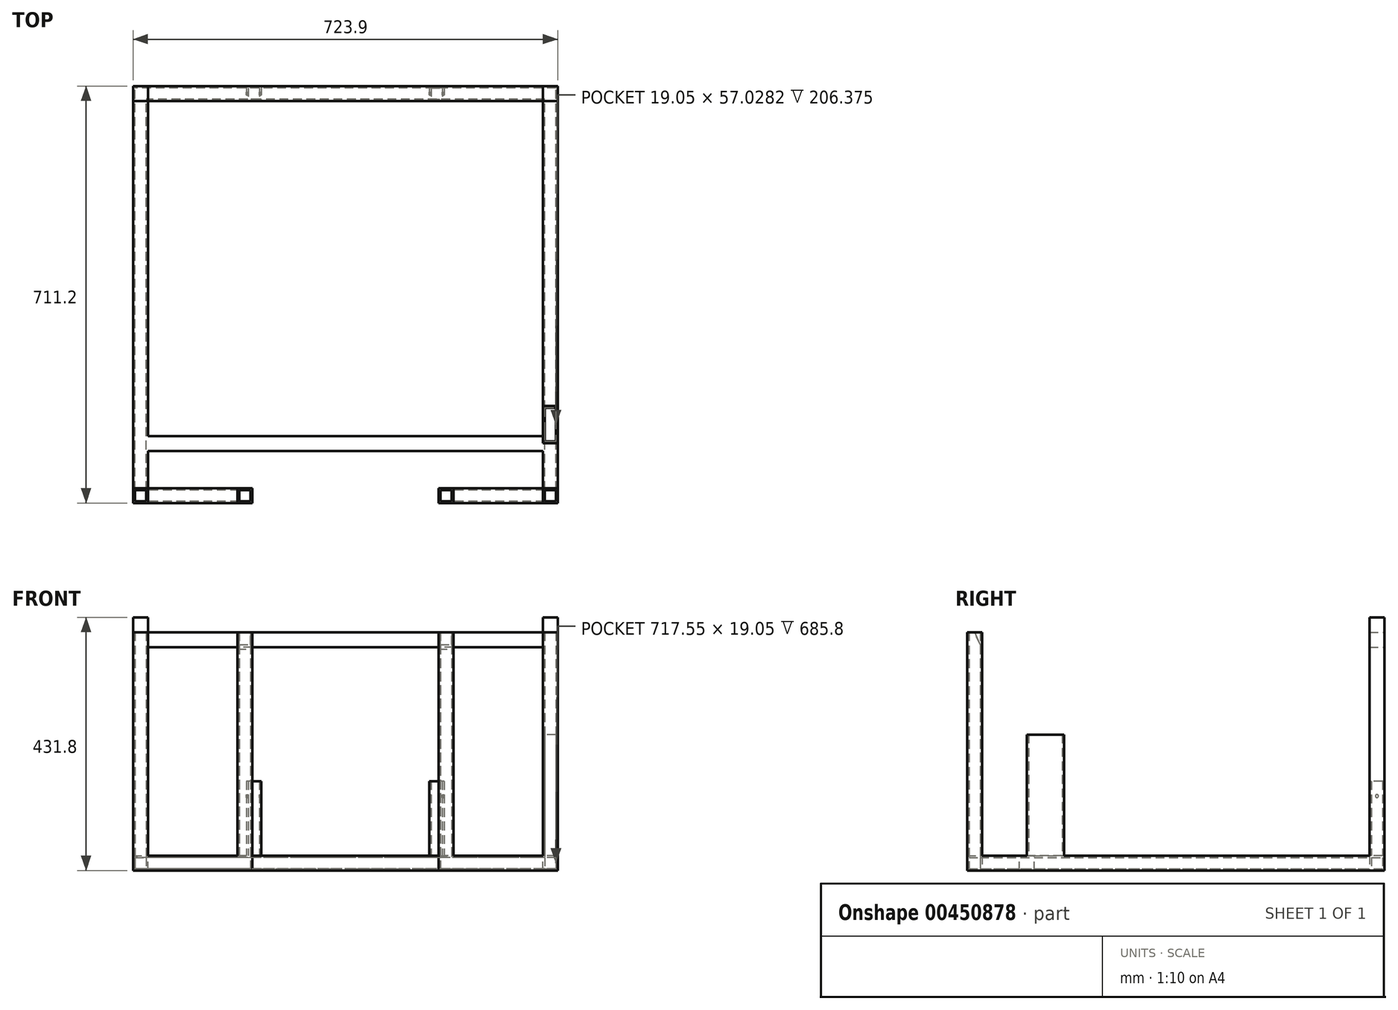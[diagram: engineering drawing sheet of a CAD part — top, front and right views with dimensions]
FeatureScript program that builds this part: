
annotation { "Feature Type Name" : "Feature", "Feature Type Description" : "" }
export const myFeature = defineFeature(function(context is Context, id is Id, definition is map)
    precondition{}
    {
        {
            var Q0;
            Q0=qCreatedBy(makeId("Top.planeOp"),FACE);
            var sketch = newSketch(context, id + "F0", { "sketchPlane" : qUnion([Q0])});
            skLineSegment(sketch, "E0.bottom", {"start": v(336.55, -330.2) * mm, "end": v(-336.55, -330.2) * mm});
            skLineSegment(sketch, "E0.top", {"start": v(336.55, 330.2) * mm, "end": v(-336.55, 330.2) * mm});
            skLineSegment(sketch, "E0.left", {"start": v(336.55, -330.2) * mm, "end": v(336.55, 330.2) * mm});
            skLineSegment(sketch, "E0.right", {"start": v(-336.55, -330.2) * mm, "end": v(-336.55, 330.2) * mm});
            skPoint(sketch, "E0.middle", {"position": v(0, 0) * mm});
            skLineSegment(sketch, "E1.bottom", {"start": v(361.95, -355.6) * mm, "end": v(-361.95, -355.6) * mm});
            skLineSegment(sketch, "E1.top", {"start": v(361.95, 355.6) * mm, "end": v(-361.95, 355.6) * mm});
            skLineSegment(sketch, "E1.left", {"start": v(361.95, -355.6) * mm, "end": v(361.95, 355.6) * mm});
            skLineSegment(sketch, "E1.right", {"start": v(-361.95, -355.6) * mm, "end": v(-361.95, 355.6) * mm});
            skSolve(sketch);
        }
        {
            var Q0;
            Q0=qSketchRegion(id+"F0",true);
            extrude(context, id + "F1", {"entities" : qUnion([Q0]), "depth" : 25.4 * mm});
        }
        {
            var Q0;
            Q0=makeQuery(id+"F1.opExtrude","CAP_FACE",FACE,{"disambiguationData":[OSD([sQuery(id+"F0.wireOp",EDGE,"E0.bottom"),sQuery(id+"F0.wireOp",EDGE,"E0.top"),sQuery(id+"F0.wireOp",EDGE,"E0.left"),sQuery(id+"F0.wireOp",EDGE,"E0.right"),sQuery(id+"F0.wireOp",EDGE,"E1.bottom"),sQuery(id+"F0.wireOp",EDGE,"E1.top"),sQuery(id+"F0.wireOp",EDGE,"E1.left"),sQuery(id+"F0.wireOp",EDGE,"E1.right")])],"isStart":false});
            var sketch = newSketch(context, id + "F2", { "sketchPlane" : qUnion([Q0])});
            skLineSegment(sketch, "E2.bottom", {"start": v(-361.95, -355.6) * mm, "end": v(-336.55, -355.6) * mm});
            skLineSegment(sketch, "E2.top", {"start": v(-361.95, -330.2) * mm, "end": v(-336.55, -330.2) * mm});
            skLineSegment(sketch, "E2.left", {"start": v(-361.95, -355.6) * mm, "end": v(-361.95, -330.2) * mm});
            skLineSegment(sketch, "E2.right", {"start": v(-336.55, -355.6) * mm, "end": v(-336.55, -330.2) * mm});
            skLineSegment(sketch, "E3.bottom", {"start": v(361.95, -355.6) * mm, "end": v(336.55, -355.6) * mm});
            skLineSegment(sketch, "E3.top", {"start": v(361.95, -330.2) * mm, "end": v(336.55, -330.2) * mm});
            skLineSegment(sketch, "E3.left", {"start": v(361.95, -355.6) * mm, "end": v(361.95, -330.2) * mm});
            skLineSegment(sketch, "E3.right", {"start": v(336.55, -355.6) * mm, "end": v(336.55, -330.2) * mm});
            skSolve(sketch);
        }
        {
            var Q0;
            Q0=makeQuery(id+"F2.imprint","IMPRINT",FACE,{"disambiguationData":[TD([[makeQuery(id+"F2.imprint","IMPRINT",EDGE,{"derivedFrom":sQuery(id+"F2.wireOp",EDGE,"E2.bottom")}),-1.0]])]});
            var Q1;
            Q1=makeQuery(id+"F2.imprint","IMPRINT",FACE,{"disambiguationData":[TD([[makeQuery(id+"F2.imprint","IMPRINT",EDGE,{"derivedFrom":sQuery(id+"F2.wireOp",EDGE,"E3.bottom")}),-1.0]])]});
            extrude(context, id + "F3", {"entities" : qUnion([Q0, Q1]), "operationType" : NewBodyOperationType.ADD, "depth" : 381 * mm});
        }
        {
            var Q0;
            {var subQ0=sQuery(id+"F0.wireOp",EDGE,"E0.left");var subQ1=sQuery(id+"F0.wireOp",EDGE,"E1.bottom");var subQ2=sQuery(id+"F0.wireOp",EDGE,"E0.bottom");var subQ3=sQuery(id+"F0.wireOp",EDGE,"E0.right");var subQ4=makeQuery(id+"F1.opExtrude","CAP_FACE",FACE,{"disambiguationData":[OSD([subQ2,sQuery(id+"F0.wireOp",EDGE,"E0.top"),subQ0,subQ3,subQ1,sQuery(id+"F0.wireOp",EDGE,"E1.top"),sQuery(id+"F0.wireOp",EDGE,"E1.left"),sQuery(id+"F0.wireOp",EDGE,"E1.right")])],"isStart":false});Q0=makeQuery(id+"F3.boolean.opBoolean","SPLIT",FACE,{"disambiguationData":[TD([makeQuery(id+"F1.opExtrude","SWEPT_FACE",FACE,{"disambiguationData":[OSD([subQ1])]})])],"derivedFrom":subQ4});}
            var sketch = newSketch(context, id + "F4", { "sketchPlane" : qUnion([Q0])});
            skLineSegment(sketch, "E4.bottom", {"start": v(-184.15, -355.6) * mm, "end": v(-158.75, -355.6) * mm});
            skLineSegment(sketch, "E4.top", {"start": v(-184.15, -330.2) * mm, "end": v(-158.75, -330.2) * mm});
            skLineSegment(sketch, "E4.left", {"start": v(-184.15, -355.6) * mm, "end": v(-184.15, -330.2) * mm});
            skLineSegment(sketch, "E4.right", {"start": v(-158.75, -355.6) * mm, "end": v(-158.75, -330.2) * mm});
            skLineSegment(sketch, "E5.MirrorCS", {"start": v(184.15, -355.6) * mm, "end": v(184.15, -330.2) * mm});
            skLineSegment(sketch, "E6.MirrorCS", {"start": v(184.15, -330.2) * mm, "end": v(158.75, -330.2) * mm});
            skLineSegment(sketch, "E7.MirrorCS", {"start": v(158.75, -355.6) * mm, "end": v(158.75, -330.2) * mm});
            skLineSegment(sketch, "E8.MirrorCS", {"start": v(184.15, -355.6) * mm, "end": v(158.75, -355.6) * mm});
            skSolve(sketch);
        }
        {
            var Q0;
            Q0=makeQuery(id+"F4.imprint","IMPRINT",FACE,{"disambiguationData":[TD([[makeQuery(id+"F4.imprint","IMPRINT",EDGE,{"derivedFrom":sQuery(id+"F4.wireOp",EDGE,"E4.bottom")}),-1.0]])]});
            var Q1;
            Q1=makeQuery(id+"F4.imprint","IMPRINT",FACE,{"disambiguationData":[TD([[makeQuery(id+"F4.imprint","IMPRINT",EDGE,{"derivedFrom":sQuery(id+"F4.wireOp",EDGE,"E5.MirrorCS")}),1.0]])]});
            extrude(context, id + "F5", {"entities" : qUnion([Q0, Q1]), "operationType" : NewBodyOperationType.ADD, "depth" : 381 * mm});
        }
        {
            var Q0;
            {var subQ0=sQuery(id+"F0.wireOp",EDGE,"E1.right");var subQ1=sQuery(id+"F0.wireOp",EDGE,"E1.left");var subQ2=sQuery(id+"F0.wireOp",EDGE,"E1.top");var subQ3=sQuery(id+"F0.wireOp",EDGE,"E0.right");var subQ4=sQuery(id+"F0.wireOp",EDGE,"E0.bottom");var subQ5=sQuery(id+"F0.wireOp",EDGE,"E0.left");var subQ6=sQuery(id+"F0.wireOp",EDGE,"E0.top");var subQ7=makeQuery(id+"F1.opExtrude","CAP_FACE",FACE,{"disambiguationData":[OSD([subQ4,subQ6,subQ5,subQ3,sQuery(id+"F0.wireOp",EDGE,"E1.bottom"),subQ2,subQ1,subQ0])],"isStart":false});Q0=makeQuery(id+"F3.boolean.opBoolean","SPLIT",FACE,{"disambiguationData":[TD([makeQuery(id+"F1.opExtrude","SWEPT_FACE",FACE,{"disambiguationData":[OSD([subQ6])]})])],"derivedFrom":subQ7});}
            var sketch = newSketch(context, id + "F6", { "sketchPlane" : qUnion([Q0])});
            skLineSegment(sketch, "E9.bottom", {"start": v(-336.55, -241.3) * mm, "end": v(336.55, -241.3) * mm});
            skLineSegment(sketch, "E9.top", {"start": v(-336.55, -266.7) * mm, "end": v(336.55, -266.7) * mm});
            skLineSegment(sketch, "E9.left", {"start": v(-336.55, -241.3) * mm, "end": v(-336.55, -266.7) * mm});
            skLineSegment(sketch, "E9.right", {"start": v(336.55, -241.3) * mm, "end": v(336.55, -266.7) * mm});
            skSolve(sketch);
        }
        {
            var Q0;
            Q0=makeQuery(id+"F6.imprint","IMPRINT",FACE,{"disambiguationData":[TD([[makeQuery(id+"F6.imprint","IMPRINT",EDGE,{"derivedFrom":sQuery(id+"F6.wireOp",EDGE,"E9.bottom")}),-1.0]])]});
            extrude(context, id + "F7", {"entities" : qUnion([Q0]), "oppositeDirection" : true, "depth" : 25.4 * mm});
        }
        {
            var Q0;
            {var subQ2=sQuery(id+"F0.wireOp",EDGE,"E1.bottom");var subQ3=makeQuery(id+"F1.opExtrude","SWEPT_FACE",FACE,{"disambiguationData":[OSD([subQ2])]});var subQ4=sQuery(id+"F0.wireOp",EDGE,"E0.bottom");var subQ6=sQuery(id+"F0.wireOp",EDGE,"E0.left");var subQ7=sQuery(id+"F0.wireOp",EDGE,"E0.right");var subQ8=makeQuery(id+"F1.opExtrude","CAP_FACE",FACE,{"disambiguationData":[OSD([subQ4,sQuery(id+"F0.wireOp",EDGE,"E0.top"),subQ6,subQ7,subQ2,sQuery(id+"F0.wireOp",EDGE,"E1.top"),sQuery(id+"F0.wireOp",EDGE,"E1.left"),sQuery(id+"F0.wireOp",EDGE,"E1.right")])],"isStart":false});Q0=makeQuery(id+"F5.boolean.opBoolean","SPLIT",FACE,{"disambiguationData":[TD([makeQuery(id+"F5.opExtrude","SWEPT_FACE",FACE,{"disambiguationData":[OSD([sQuery(id+"F4.wireOp",EDGE,"E4.right")])]})])],"derivedFrom":makeQuery(id+"F3.boolean.opBoolean","SPLIT",FACE,{"disambiguationData":[TD([subQ3])],"derivedFrom":subQ8})});}
            var sketch = newSketch(context, id + "F8", { "sketchPlane" : qUnion([Q0])});
            skLineSegment(sketch, "E10.bottom", {"start": v(-158.75, -330.2) * mm, "end": v(158.75, -330.2) * mm});
            skLineSegment(sketch, "E10.top", {"start": v(-158.75, -355.6) * mm, "end": v(158.75, -355.6) * mm});
            skLineSegment(sketch, "E10.left", {"start": v(-158.75, -330.2) * mm, "end": v(-158.75, -355.6) * mm});
            skLineSegment(sketch, "E10.right", {"start": v(158.75, -330.2) * mm, "end": v(158.75, -355.6) * mm});
            skSolve(sketch);
        }
        {
            var Q0;
            Q0=makeQuery(id+"F8.imprint","IMPRINT",FACE,{"disambiguationData":[TD([[makeQuery(id+"F8.imprint","IMPRINT",EDGE,{"derivedFrom":sQuery(id+"F8.wireOp",EDGE,"E10.bottom")}),1.0]])]});
            extrude(context, id + "F9", {"entities" : qUnion([Q0]), "operationType" : NewBodyOperationType.REMOVE, "oppositeDirection" : true, "depth" : 25.4 * mm});
        }
        {
            var Q0;
            Q0=makeQuery(id+"F3.opExtrude","CAP_FACE",FACE,{"disambiguationData":[OSD([sQuery(id+"F2.wireOp",EDGE,"E2.bottom"),sQuery(id+"F2.wireOp",EDGE,"E2.top"),sQuery(id+"F2.wireOp",EDGE,"E2.left"),sQuery(id+"F2.wireOp",EDGE,"E2.right")])],"isStart":false});
            var Q1;
            Q1=makeQuery(id+"F5.opExtrude","CAP_FACE",FACE,{"disambiguationData":[OSD([sQuery(id+"F4.wireOp",EDGE,"E4.bottom"),sQuery(id+"F4.wireOp",EDGE,"E4.top"),sQuery(id+"F4.wireOp",EDGE,"E4.left"),sQuery(id+"F4.wireOp",EDGE,"E4.right")])],"isStart":false});
            var Q2;
            Q2=makeQuery(id+"F5.opExtrude","CAP_FACE",FACE,{"disambiguationData":[OSD([sQuery(id+"F4.wireOp",EDGE,"E5.MirrorCS"),sQuery(id+"F4.wireOp",EDGE,"E6.MirrorCS"),sQuery(id+"F4.wireOp",EDGE,"E7.MirrorCS"),sQuery(id+"F4.wireOp",EDGE,"E8.MirrorCS")])],"isStart":false});
            var Q3;
            Q3=makeQuery(id+"F3.opExtrude","CAP_FACE",FACE,{"disambiguationData":[OSD([sQuery(id+"F2.wireOp",EDGE,"E3.bottom"),sQuery(id+"F2.wireOp",EDGE,"E3.top"),sQuery(id+"F2.wireOp",EDGE,"E3.left"),sQuery(id+"F2.wireOp",EDGE,"E3.right")])],"isStart":false});
            shell(context, id + "F10", {"entities" : qUnion([Q0, Q1, Q2, Q3]), "thickness" : 3.17 * mm});
        }
        {
            var Q0;
            {var subQ0=sQuery(id+"F0.wireOp",EDGE,"E1.right");var subQ1=sQuery(id+"F0.wireOp",EDGE,"E1.left");var subQ2=sQuery(id+"F0.wireOp",EDGE,"E1.top");var subQ3=sQuery(id+"F0.wireOp",EDGE,"E0.right");var subQ4=sQuery(id+"F0.wireOp",EDGE,"E0.bottom");var subQ5=sQuery(id+"F0.wireOp",EDGE,"E0.left");var subQ6=sQuery(id+"F0.wireOp",EDGE,"E0.top");var subQ7=makeQuery(id+"F1.opExtrude","CAP_FACE",FACE,{"disambiguationData":[OSD([subQ4,subQ6,subQ5,subQ3,sQuery(id+"F0.wireOp",EDGE,"E1.bottom"),subQ2,subQ1,subQ0])],"isStart":false});Q0=makeQuery(id+"F3.boolean.opBoolean","SPLIT",FACE,{"disambiguationData":[TD([makeQuery(id+"F1.opExtrude","SWEPT_FACE",FACE,{"disambiguationData":[OSD([subQ6])]})])],"derivedFrom":subQ7});}
            var sketch = newSketch(context, id + "F11", { "sketchPlane" : qUnion([Q0])});
            skLineSegment(sketch, "E11.bottom", {"start": v(361.95, 355.6) * mm, "end": v(336.55, 355.6) * mm});
            skLineSegment(sketch, "E11.top", {"start": v(361.95, 330.2) * mm, "end": v(336.55, 330.2) * mm});
            skLineSegment(sketch, "E11.left", {"start": v(361.95, 355.6) * mm, "end": v(361.95, 330.2) * mm});
            skLineSegment(sketch, "E11.right", {"start": v(336.55, 355.6) * mm, "end": v(336.55, 330.2) * mm});
            skLineSegment(sketch, "E12.bottom", {"start": v(-361.95, 355.6) * mm, "end": v(-336.55, 355.6) * mm});
            skLineSegment(sketch, "E12.top", {"start": v(-361.95, 330.2) * mm, "end": v(-336.55, 330.2) * mm});
            skLineSegment(sketch, "E12.left", {"start": v(-361.95, 355.6) * mm, "end": v(-361.95, 330.2) * mm});
            skLineSegment(sketch, "E12.right", {"start": v(-336.55, 355.6) * mm, "end": v(-336.55, 330.2) * mm});
            skSolve(sketch);
        }
        {
            var Q0;
            Q0=makeQuery(id+"F11.imprint","IMPRINT",FACE,{"disambiguationData":[TD([[makeQuery(id+"F11.imprint","IMPRINT",EDGE,{"derivedFrom":sQuery(id+"F11.wireOp",EDGE,"E11.bottom")}),1.0]])]});
            var Q1;
            Q1=makeQuery(id+"F11.imprint","IMPRINT",FACE,{"disambiguationData":[TD([[makeQuery(id+"F11.imprint","IMPRINT",EDGE,{"derivedFrom":sQuery(id+"F11.wireOp",EDGE,"E12.bottom")}),1.0]])]});
            extrude(context, id + "F12", {"entities" : qUnion([Q0, Q1]), "operationType" : NewBodyOperationType.ADD, "depth" : 406.4 * mm});
        }
        {
            var Q0;
            Q0=makeQuery(id+"F12.opExtrude","SWEPT_FACE",FACE,{"disambiguationData":[OSD([sQuery(id+"F11.wireOp",EDGE,"E12.right")])]});
            var sketch = newSketch(context, id + "F13", { "sketchPlane" : qUnion([Q0])});
            skLineSegment(sketch, "E13.bottom", {"start": v(330.2, 406.4) * mm, "end": v(355.6, 406.4) * mm});
            skLineSegment(sketch, "E13.top", {"start": v(330.2, 381) * mm, "end": v(355.6, 381) * mm});
            skLineSegment(sketch, "E13.left", {"start": v(330.2, 406.4) * mm, "end": v(330.2, 381) * mm});
            skLineSegment(sketch, "E13.right", {"start": v(355.6, 406.4) * mm, "end": v(355.6, 381) * mm});
            skSolve(sketch);
        }
        {
            var Q0;
            Q0=makeQuery(id+"F13.imprint","IMPRINT",FACE,{"disambiguationData":[TD([[makeQuery(id+"F13.imprint","IMPRINT",EDGE,{"derivedFrom":sQuery(id+"F13.wireOp",EDGE,"E13.bottom")}),-1.0]])]});
            extrude(context, id + "F14", {"entities" : qUnion([Q0]), "operationType" : NewBodyOperationType.ADD, "depth" : 673.1 * mm});
        }
        {
            var Q0;
            {var subQ2=sQuery(id+"F0.wireOp",EDGE,"E1.left");var subQ3=makeQuery(id+"F1.opExtrude","SWEPT_FACE",FACE,{"disambiguationData":[OSD([subQ2])]});var subQ5=sQuery(id+"F0.wireOp",EDGE,"E0.bottom");var subQ7=sQuery(id+"F0.wireOp",EDGE,"E1.right");var subQ8=sQuery(id+"F0.wireOp",EDGE,"E1.top");var subQ9=sQuery(id+"F0.wireOp",EDGE,"E0.right");var subQ10=sQuery(id+"F0.wireOp",EDGE,"E0.left");var subQ11=sQuery(id+"F0.wireOp",EDGE,"E0.top");var subQ12=makeQuery(id+"F1.opExtrude","CAP_FACE",FACE,{"disambiguationData":[OSD([subQ5,subQ11,subQ10,subQ9,sQuery(id+"F0.wireOp",EDGE,"E1.bottom"),subQ8,subQ2,subQ7])],"isStart":false});var subQ13=makeQuery(id+"F1.opExtrude","SWEPT_FACE",FACE,{"disambiguationData":[OSD([subQ11])]});Q0=makeQuery(id+"F12.boolean.opBoolean","SPLIT",FACE,{"disambiguationData":[TD([subQ3])],"derivedFrom":makeQuery(id+"F3.boolean.opBoolean","SPLIT",FACE,{"disambiguationData":[TD([subQ13])],"derivedFrom":subQ12})});}
            var sketch = newSketch(context, id + "F15", { "sketchPlane" : qUnion([Q0])});
            skLineSegment(sketch, "E14.bottom", {"start": v(361.95, -190.42) * mm, "end": v(336.55, -190.42) * mm});
            skLineSegment(sketch, "E14.top", {"start": v(361.95, -253.8) * mm, "end": v(336.55, -253.8) * mm});
            skLineSegment(sketch, "E14.left", {"start": v(361.95, -190.42) * mm, "end": v(361.95, -253.8) * mm});
            skLineSegment(sketch, "E14.right", {"start": v(336.55, -190.42) * mm, "end": v(336.55, -253.8) * mm});
            skLineSegment(sketch, "E15.0", {"start": v(358.78, -193.6) * mm, "end": v(339.73, -193.6) * mm});
            skLineSegment(sketch, "E15.1", {"start": v(358.78, -193.6) * mm, "end": v(358.78, -250.62) * mm});
            skLineSegment(sketch, "E15.2", {"start": v(358.78, -250.62) * mm, "end": v(339.73, -250.62) * mm});
            skLineSegment(sketch, "E15.3", {"start": v(339.73, -193.6) * mm, "end": v(339.73, -250.62) * mm});
            skSolve(sketch);
        }
        {
            var Q0;
            Q0=qSketchRegion(id+"F15",true);
            extrude(context, id + "F16", {"entities" : qUnion([Q0]), "operationType" : NewBodyOperationType.ADD, "depth" : 206.38 * mm});
        }
        {
            var Q0;
            {var subQ0=sQuery(id+"F0.wireOp",EDGE,"E1.top");var subQ1=makeQuery(id+"F1.opExtrude","SWEPT_FACE",FACE,{"disambiguationData":[OSD([subQ0])]});var subQ2=sQuery(id+"F0.wireOp",EDGE,"E1.right");var subQ3=sQuery(id+"F0.wireOp",EDGE,"E1.left");var subQ4=sQuery(id+"F0.wireOp",EDGE,"E0.right");var subQ5=sQuery(id+"F0.wireOp",EDGE,"E0.left");var subQ6=sQuery(id+"F0.wireOp",EDGE,"E0.top");var subQ7=sQuery(id+"F0.wireOp",EDGE,"E0.bottom");var subQ8=makeQuery(id+"F1.opExtrude","CAP_FACE",FACE,{"disambiguationData":[OSD([subQ7,subQ6,subQ5,subQ4,sQuery(id+"F0.wireOp",EDGE,"E1.bottom"),subQ0,subQ3,subQ2])],"isStart":false});var subQ9=makeQuery(id+"F1.opExtrude","SWEPT_FACE",FACE,{"disambiguationData":[OSD([subQ6])]});Q0=makeQuery(id+"F12.boolean.opBoolean","SPLIT",FACE,{"disambiguationData":[TD([subQ1])],"derivedFrom":makeQuery(id+"F3.boolean.opBoolean","SPLIT",FACE,{"disambiguationData":[TD([subQ9])],"derivedFrom":subQ8})});}
            var sketch = newSketch(context, id + "F17", { "sketchPlane" : qUnion([Q0])});
            skLineSegment(sketch, "E16.bottom", {"start": v(-143, 355.6) * mm, "end": v(143, 355.6) * mm, "construction": true});
            skLineSegment(sketch, "E16.top", {"start": v(-143, 330.2) * mm, "end": v(143, 330.2) * mm, "construction": true});
            skLineSegment(sketch, "E16.left", {"start": v(-143, 355.6) * mm, "end": v(-143, 330.2) * mm});
            skLineSegment(sketch, "E16.right", {"start": v(143, 355.6) * mm, "end": v(143, 330.2) * mm});
            skLineSegment(sketch, "E17", {"start": v(0, 355.6) * mm, "end": v(0, 330.2) * mm, "construction": true});
            skLineSegment(sketch, "E18.bottom", {"start": v(-143, 355.6) * mm, "end": v(-168.4, 355.6) * mm});
            skLineSegment(sketch, "E18.top", {"start": v(-143, 330.2) * mm, "end": v(-168.4, 330.2) * mm});
            skLineSegment(sketch, "E18.right", {"start": v(-168.4, 355.6) * mm, "end": v(-168.4, 330.2) * mm});
            skLineSegment(sketch, "E19.bottom", {"start": v(143, 355.6) * mm, "end": v(168.4, 355.6) * mm});
            skLineSegment(sketch, "E19.top", {"start": v(143, 330.2) * mm, "end": v(168.4, 330.2) * mm});
            skLineSegment(sketch, "E19.right", {"start": v(168.4, 355.6) * mm, "end": v(168.4, 330.2) * mm});
            skLineSegment(sketch, "E20.0", {"start": v(-146.18, 352.43) * mm, "end": v(-146.18, 333.38) * mm});
            skLineSegment(sketch, "E20.1", {"start": v(-146.18, 352.43) * mm, "end": v(-165.23, 352.43) * mm});
            skLineSegment(sketch, "E20.2", {"start": v(-165.23, 352.43) * mm, "end": v(-165.23, 333.38) * mm});
            skLineSegment(sketch, "E20.3", {"start": v(-146.18, 333.38) * mm, "end": v(-165.23, 333.38) * mm});
            skLineSegment(sketch, "E21.0", {"start": v(146.18, 352.43) * mm, "end": v(165.23, 352.43) * mm});
            skLineSegment(sketch, "E21.1", {"start": v(146.18, 352.43) * mm, "end": v(146.18, 333.38) * mm});
            skLineSegment(sketch, "E21.2", {"start": v(146.18, 333.38) * mm, "end": v(165.23, 333.38) * mm});
            skLineSegment(sketch, "E21.3", {"start": v(165.23, 352.43) * mm, "end": v(165.23, 333.38) * mm});
            skSolve(sketch);
        }
        {
            var Q0;
            Q0 = qSketchRegion(id + "F17", true);
            extrude(context, id + "F18", {"entities" : qUnion([Q0]), "operationType" : NewBodyOperationType.ADD, "depth" : 127 * mm});
        }
        {
            var Q0;
            Q0=makeQuery(id+"F18.opExtrude","SWEPT_FACE",FACE,{"disambiguationData":[OSD([sQuery(id+"F17.wireOp",EDGE,"E19.right")])]});
            var sketch = newSketch(context, id + "F19", { "sketchPlane" : qUnion([Q0])});
            skLineSegment(sketch, "E22", {"start": v(342.9, 152.4) * mm, "end": v(342.9, 25.4) * mm, "construction": true});
            skPoint(sketch, "E23", {"position": v(342.9, 127) * mm});
            skSolve(sketch);
        }
        {
            var Q0;
            Q0=sQuery(id+"F19.wireOp",VERTEX,"E23");
            var Q1;
            Q1=makeQuery(id+"F1.opExtrude","SWEPT_BODY",BODY,{"disambiguationData":[OSD([sQuery(id+"F0.wireOp",EDGE,"E0.bottom"),sQuery(id+"F0.wireOp",EDGE,"E0.top"),sQuery(id+"F0.wireOp",EDGE,"E0.left"),sQuery(id+"F0.wireOp",EDGE,"E0.right"),sQuery(id+"F0.wireOp",EDGE,"E1.bottom"),sQuery(id+"F0.wireOp",EDGE,"E1.top"),sQuery(id+"F0.wireOp",EDGE,"E1.left"),sQuery(id+"F0.wireOp",EDGE,"E1.right")])]});
            hole(context, id + "F20", {"style" : HoleStyle.SIMPLE, "endStyle" : HoleEndStyle.BLIND, "holeDiameter" : 5.1 * mm, "holeDepth" : 406.4 * mm, "isTappedThrough" : true, "tappedDepth" : 12.7 * mm, "tapClearance" : 3, "locations" : qUnion([Q0]), "scope" : qUnion([Q1])});
        }
        {
            var Q0;
            Q0=makeQuery(id+"F5.opExtrude","SWEPT_FACE",FACE,{"disambiguationData":[OSD([sQuery(id+"F4.wireOp",EDGE,"E5.MirrorCS")])]});
            var sketch = newSketch(context, id + "F21", { "sketchPlane" : qUnion([Q0])});
            skLineSegment(sketch, "E24", {"start": v(-342.9, 406.4) * mm, "end": v(-303.12, 316.63) * mm});
            skLineSegment(sketch, "E25", {"start": v(-303.12, 316.63) * mm, "end": v(-308.57, 412.87) * mm});
            skLineSegment(sketch, "E26", {"start": v(-308.57, 412.87) * mm, "end": v(-351.54, 424.67) * mm});
            skLineSegment(sketch, "E27", {"start": v(-351.54, 424.67) * mm, "end": v(-342.9, 406.4) * mm});
            skSolve(sketch);
        }
        {
            var Q0;
            Q0 = qSketchRegion(id + "F21", true);
            extrude(context, id + "F22", {"entities" : qUnion([Q0]), "operationType" : NewBodyOperationType.REMOVE, "oppositeDirection" : true, "depth" : 406.4 * mm});
        }
    });
